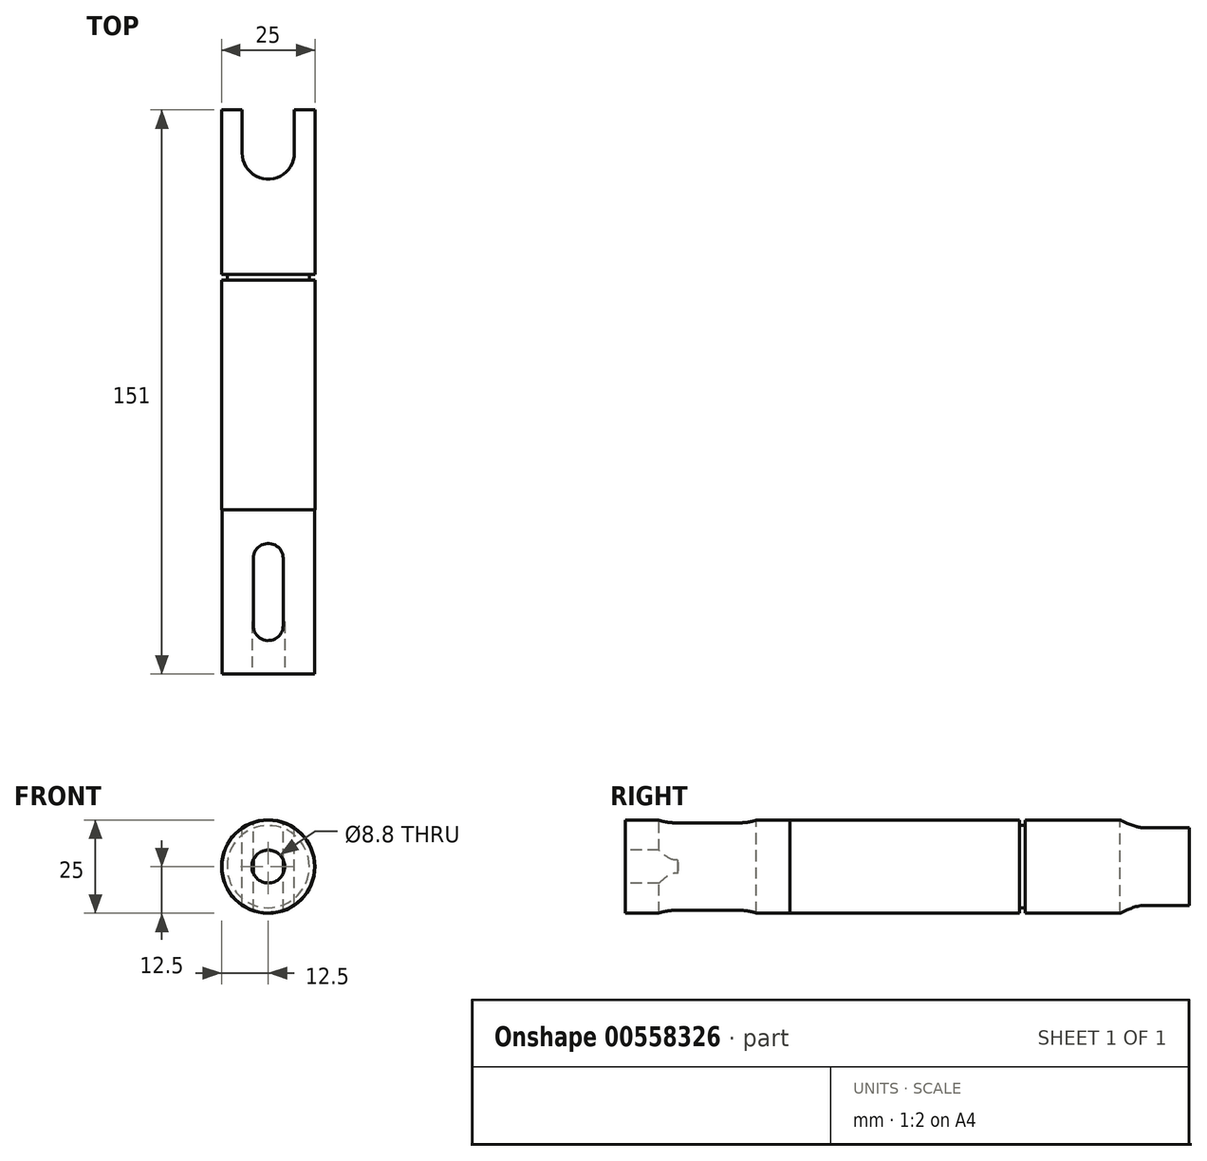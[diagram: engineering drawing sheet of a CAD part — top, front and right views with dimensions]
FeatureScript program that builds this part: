
annotation { "Feature Type Name" : "Feature", "Feature Type Description" : "" }
export const myFeature = defineFeature(function(context is Context, id is Id, definition is map)
    precondition{}
    {
        {
            var Q0;
            Q0=qCreatedBy(makeId("Front.planeOp"),FACE);
            var sketch = newSketch(context, id + "F0", { "sketchPlane" : qUnion([Q0])});
            skCircle(sketch, "E0", {"center": v(0, 0) * mm, "radius": 12.5 * mm});
            skSolve(sketch);
        }
        {
            var Q0;
            Q0=makeQuery(id+"F0.imprint","IMPRINT",FACE,{"disambiguationData":[TD([[makeQuery(id+"F0.imprint","IMPRINT",EDGE,{"derivedFrom":sQuery(id+"F0.wireOp",EDGE,"E0")}),1.0]])]});
            extrude(context, id + "F1", {"entities" : qUnion([Q0]), "endBound" : BoundingType.SYMMETRIC, "depth" : 107 * mm, "offsetDistance" : 25 * mm});
        }
        {
            var Q0;
            Q0=qCreatedBy(makeId("Top.planeOp"),FACE);
            var sketch = newSketch(context, id + "F2", { "sketchPlane" : qUnion([Q0])});
            skLineSegment(sketch, "E1", {"start": v(0, 53.5) * mm, "end": v(0, 42) * mm});
            skArc(sketch, "E2", {"start": v(0, 35) * mm, "mid": v(-4.95, 37.05) * mm, "end": v(-7, 42) * mm});
            skArc(sketch, "E3", {"start": v(0, 35) * mm, "mid": v(4.95, 37.05) * mm, "end": v(7, 42) * mm});
            skLineSegment(sketch, "E4", {"start": v(-7, 42) * mm, "end": v(-7, 54.22) * mm});
            skLineSegment(sketch, "E5", {"start": v(7, 42) * mm, "end": v(7, 54.22) * mm});
            skLineSegment(sketch, "E6", {"start": v(-7, 54.22) * mm, "end": v(7, 54.22) * mm});
            skSolve(sketch);
        }
        {
            var Q0;
            {var subQ0=sQuery(id+"F0.wireOp",EDGE,"E0");Q0=makeQuery(id+"FyShQfCp6cq0NDm_1.boolean.opBoolean","SPLIT",FACE,{"disambiguationData":[TD([makeQuery(id+"FyShQfCp6cq0NDm_1.opExtrude","SWEPT_FACE",FACE,{"disambiguationData":[OSD([sQuery(id+"F2.wireOp",EDGE,"E5")])]})])],"derivedFrom":makeQuery(id+"F1.opExtrude","CAP_FACE",FACE,{"disambiguationData":[OSD([subQ0])],"isStart":true})});}
            var sketch = newSketch(context, id + "F3", { "sketchPlane" : qUnion([Q0])});
            skCircle(sketch, "E7", {"center": v(0, 0) * mm, "radius": 11 * mm});
            skCircle(sketch, "E8", {"center": v(0, 0) * mm, "radius": 12.5 * mm});
            skSolve(sketch);
        }
        {
            var Q0;
            {var subQ4=sQuery(id+"F3.wireOp",EDGE,"E8");Q0=makeQuery(id+"F3.imprint","IMPRINT",FACE,{"disambiguationData":[TD([[makeQuery(id+"F3.imprint","IMPRINT",EDGE,{"disambiguationData":[OD(1.0)],"derivedFrom":subQ4}),-1.0]])]});}
            var Q1;
            {var subQ4=sQuery(id+"F3.wireOp",EDGE,"E8");Q1=makeQuery(id+"F3.imprint","IMPRINT",FACE,{"disambiguationData":[TD([[makeQuery(id+"F3.imprint","IMPRINT",EDGE,{"disambiguationData":[OD(0.0)],"derivedFrom":subQ4}),1.0]])]});}
            extrude(context, id + "F4", {"entities" : qUnion([Q0, Q1]), "operationType" : NewBodyOperationType.REMOVE, "oppositeDirection" : true, "depth" : 44 * mm + 1.5 * mm, "offsetDistance" : 25 * mm});
        }
        {
            var Q0;
            Q0 = qSketchRegion(id + "F3", true);
            extrude(context, id + "F5", {"entities" : qUnion([Q0]), "operationType" : NewBodyOperationType.ADD, "oppositeDirection" : true, "depth" : 44 * mm, "offsetDistance" : 25 * mm});
        }
        {
            var Q0;
            Q0 = qSketchRegion(id + "F2", true);
            extrude(context, id + "F6", {"entities" : qUnion([Q0]), "operationType" : NewBodyOperationType.REMOVE, "endBound" : BoundingType.SYMMETRIC, "oppositeDirection" : true, "depth" : 25 * mm, "offsetDistance" : 25 * mm});
        }
        {
            var Q0;
            Q0=makeQuery(id+"F1.opExtrude","CAP_FACE",FACE,{"disambiguationData":[OSD([sQuery(id+"F0.wireOp",EDGE,"E0")])],"isStart":false});
            var sketch = newSketch(context, id + "F7", { "sketchPlane" : qUnion([Q0])});
            skCircle(sketch, "E9", {"center": v(0, 0) * mm, "radius": 12.4 * mm});
            skSolve(sketch);
        }
        {
            var Q0;
            Q0 = qSketchRegion(id + "F7", true);
            extrude(context, id + "F8", {"entities" : qUnion([Q0]), "operationType" : NewBodyOperationType.ADD, "depth" : 44 * mm, "offsetDistance" : 25 * mm});
        }
        {
            var Q0;
            Q0=makeQuery(id+"F8.opExtrude","CAP_FACE",FACE,{"disambiguationData":[OSD([sQuery(id+"F7.wireOp",EDGE,"E9")])],"isStart":false});
            var sketch = newSketch(context, id + "F9", { "sketchPlane" : qUnion([Q0])});
            skCircle(sketch, "E10", {"center": v(0, 0) * mm, "radius": 6.3 * mm});
            skSolve(sketch);
        }
        {
            var Q0;
            Q0=sQuery(id+"F9.wireOp",VERTEX,"E10.center");
            var Q1;
            Q1=makeQuery(id+"F1.opExtrude","SWEPT_BODY",BODY,{"disambiguationData":[OSD([sQuery(id+"F0.wireOp",EDGE,"E0")])]});
            hole(context, id + "F10", {"style" : HoleStyle.SIMPLE, "endStyle" : HoleEndStyle.BLIND, "standardTappedOrClearance" : lookupTablePath({ "standard" : "ISO", "fit" : "Normal", "size" : "M8", "type" : "Clearance" }), "standardBlindInLast" : lookupTablePath({ "fit" : "Standard", "standard" : "ISO", "size" : "M8", "type" : "Clearance" }), "holeDiameter" : 8.8 * mm, "holeDepth" : 14 * mm, "isTappedThrough" : true, "tappedDepth" : 12 * mm, "tapClearance" : 3, "locations" : qUnion([Q0]), "scope" : qUnion([Q1])});
        }
        {
            var Q0;
            Q0=qCreatedBy(makeId("Top.planeOp"),FACE);
            var sketch = newSketch(context, id + "F11", { "sketchPlane" : qUnion([Q0])});
            skPoint(sketch, "E11.middle", {"position": v(0, -76.98) * mm});
            skArc(sketch, "E12", {"start": v(4, -66.5) * mm, "mid": v(0, -62.5) * mm, "end": v(-4, -66.5) * mm});
            skArc(sketch, "E13", {"start": v(-4, -84.5) * mm, "mid": v(0, -88.5) * mm, "end": v(4, -84.5) * mm});
            skLineSegment(sketch, "E14", {"start": v(-4, -84.5) * mm, "end": v(-4, -66.5) * mm});
            skLineSegment(sketch, "E15", {"start": v(4, -84.5) * mm, "end": v(4, -66.5) * mm});
            skSolve(sketch);
        }
        {
            var Q0;
            Q0 = qSketchRegion(id + "F11", true);
            extrude(context, id + "F12", {"entities" : qUnion([Q0]), "operationType" : NewBodyOperationType.REMOVE, "endBound" : BoundingType.SYMMETRIC, "oppositeDirection" : true, "depth" : 25 * mm, "offsetDistance" : 25 * mm});
        }
    });
